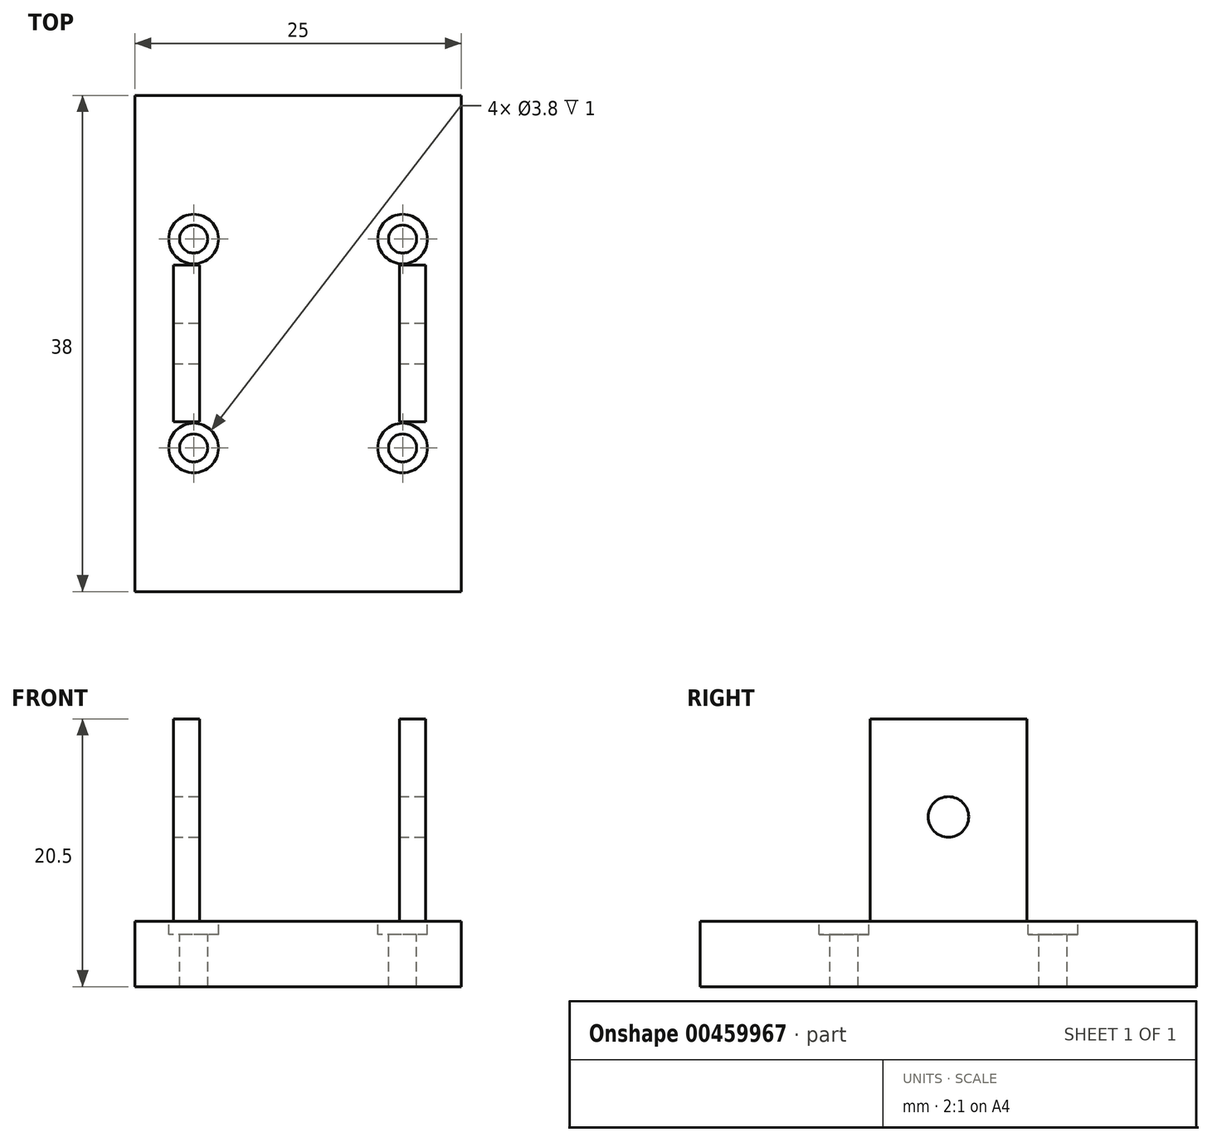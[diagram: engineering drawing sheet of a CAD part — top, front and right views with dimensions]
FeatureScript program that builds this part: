
annotation { "Feature Type Name" : "Feature", "Feature Type Description" : "" }
export const myFeature = defineFeature(function(context is Context, id is Id, definition is map)
    precondition{}
    {
        {
            var Q0;
            Q0=qCreatedBy(makeId("Top.planeOp"),FACE);
            var sketch = newSketch(context, id + "F0", { "sketchPlane" : qUnion([Q0])});
            skLineSegment(sketch, "E0.bottom", {"start": v(-18.16, 26.84) * mm, "end": v(6.84, 26.84) * mm});
            skLineSegment(sketch, "E0.top", {"start": v(-18.16, -11.16) * mm, "end": v(6.84, -11.16) * mm});
            skLineSegment(sketch, "E0.left", {"start": v(-18.16, 26.84) * mm, "end": v(-18.16, -11.16) * mm});
            skLineSegment(sketch, "E0.right", {"start": v(6.84, 26.84) * mm, "end": v(6.84, -11.16) * mm});
            skSolve(sketch);
        }
        {
            var Q0;
            Q0=makeQuery(id+"F0.imprint","IMPRINT",FACE,{"disambiguationData":[TD([[makeQuery(id+"F0.imprint","IMPRINT",EDGE,{"derivedFrom":sQuery(id+"F0.wireOp",EDGE,"E0.bottom")}),-1.0]])]});
            extrude(context, id + "F1", {"entities" : qUnion([Q0]), "depth" : 5 * mm});
        }
        {
            var Q0;
            Q0=makeQuery(id+"F1.opExtrude","CAP_FACE",FACE,{"disambiguationData":[OSD([sQuery(id+"F0.wireOp",EDGE,"E0.bottom"),sQuery(id+"F0.wireOp",EDGE,"E0.top"),sQuery(id+"F0.wireOp",EDGE,"E0.left"),sQuery(id+"F0.wireOp",EDGE,"E0.right")])],"isStart":false});
            var sketch = newSketch(context, id + "F2", { "sketchPlane" : qUnion([Q0])});
            skPoint(sketch, "E1.centerSnap0", {"position": v(-18.16, 7.84) * mm});
            skCircle(sketch, "E2", {"center": v(-13.66, 15.84) * mm, "radius": 1.07 * mm});
            skCircle(sketch, "E3", {"center": v(2.34, 15.84) * mm, "radius": 1.07 * mm});
            skCircle(sketch, "E4", {"center": v(-13.66, -0.16) * mm, "radius": 1.07 * mm});
            skCircle(sketch, "E5", {"center": v(2.34, -0.16) * mm, "radius": 1.07 * mm});
            skLineSegment(sketch, "E6.bottom", {"start": v(-13.66, 15.84) * mm, "end": v(2.34, 15.84) * mm});
            skLineSegment(sketch, "E6.top", {"start": v(-13.66, -0.16) * mm, "end": v(2.34, -0.16) * mm});
            skLineSegment(sketch, "E6.left", {"start": v(-13.66, 15.84) * mm, "end": v(-13.66, -0.16) * mm});
            skLineSegment(sketch, "E6.right", {"start": v(2.34, 15.84) * mm, "end": v(2.34, -0.16) * mm});
            skSolve(sketch);
        }
        {
            var Q0;
            {var subQ0=sQuery(id+"F2.wireOp",EDGE,"7fE2m0a1-qSu8-JNNJ-dZt4-1u2iovesNatf");var subQ1=sQuery(id+"F2.wireOp",EDGE,"E3");var subQ2=makeQuery(id+"F2.imprint","INTERSECT",VERTEX,{"derivedFrom":[subQ1,subQ0]});Q0=makeQuery(id+"F2.imprint","IMPRINT",FACE,{"disambiguationData":[TD([[makeQuery(id+"F2.imprint","IMPRINT",EDGE,{"disambiguationData":[TD([[subQ2,1.0]])],"derivedFrom":subQ1}),1.0]])]});}
            var Q1;
            {var subQ0=sQuery(id+"F2.wireOp",EDGE,"7fE2m0a1-qSu8-JNNJ-dZt4-1u2iovesNatf");var subQ1=sQuery(id+"F2.wireOp",EDGE,"E3");var subQ2=makeQuery(id+"F2.imprint","INTERSECT",VERTEX,{"derivedFrom":[subQ1,subQ0]});Q1=makeQuery(id+"F2.imprint","IMPRINT",FACE,{"disambiguationData":[TD([[makeQuery(id+"F2.imprint","IMPRINT",EDGE,{"disambiguationData":[TD([[subQ2,-1.0]])],"derivedFrom":subQ1}),1.0]])]});}
            var Q2;
            {var subQ0=sQuery(id+"F2.wireOp",EDGE,"WQd2Qh7p-ENVo-NeKd-jbVU-tQCCQaMnz0CV");var subQ1=sQuery(id+"F2.wireOp",EDGE,"E4");var subQ2=makeQuery(id+"F2.imprint","INTERSECT",VERTEX,{"derivedFrom":[subQ1,subQ0]});Q2=makeQuery(id+"F2.imprint","IMPRINT",FACE,{"disambiguationData":[TD([[makeQuery(id+"F2.imprint","IMPRINT",EDGE,{"disambiguationData":[TD([[subQ2,1.0]])],"derivedFrom":subQ1}),1.0]])]});}
            var Q3;
            {var subQ0=sQuery(id+"F2.wireOp",EDGE,"WQd2Qh7p-ENVo-NeKd-jbVU-tQCCQaMnz0CV");var subQ1=sQuery(id+"F2.wireOp",EDGE,"E4");var subQ2=makeQuery(id+"F2.imprint","INTERSECT",VERTEX,{"derivedFrom":[subQ1,subQ0]});Q3=makeQuery(id+"F2.imprint","IMPRINT",FACE,{"disambiguationData":[TD([[makeQuery(id+"F2.imprint","IMPRINT",EDGE,{"disambiguationData":[TD([[subQ2,-1.0]])],"derivedFrom":subQ1}),1.0]])]});}
            var Q4;
            {var subQ0=sQuery(id+"F2.wireOp",EDGE,"7fE2m0a1-qSu8-JNNJ-dZt4-1u2iovesNatf");var subQ1=sQuery(id+"F2.wireOp",EDGE,"E5");var subQ2=makeQuery(id+"F2.imprint","INTERSECT",VERTEX,{"derivedFrom":[subQ1,subQ0]});Q4=makeQuery(id+"F2.imprint","IMPRINT",FACE,{"disambiguationData":[TD([[makeQuery(id+"F2.imprint","IMPRINT",EDGE,{"disambiguationData":[TD([[subQ2,-1.0]])],"derivedFrom":subQ1}),1.0]])]});}
            var Q5;
            {var subQ0=sQuery(id+"F2.wireOp",EDGE,"7fE2m0a1-qSu8-JNNJ-dZt4-1u2iovesNatf");var subQ1=sQuery(id+"F2.wireOp",EDGE,"E5");var subQ2=makeQuery(id+"F2.imprint","INTERSECT",VERTEX,{"derivedFrom":[subQ1,subQ0]});Q5=makeQuery(id+"F2.imprint","IMPRINT",FACE,{"disambiguationData":[TD([[makeQuery(id+"F2.imprint","IMPRINT",EDGE,{"disambiguationData":[TD([[subQ2,1.0]])],"derivedFrom":subQ1}),1.0]])]});}
            var Q6;
            {var subQ0=sQuery(id+"F2.wireOp",EDGE,"WQd2Qh7p-ENVo-NeKd-jbVU-tQCCQaMnz0CV");var subQ1=sQuery(id+"F2.wireOp",EDGE,"E2");var subQ2=makeQuery(id+"F2.imprint","INTERSECT",VERTEX,{"derivedFrom":[subQ1,subQ0]});Q6=makeQuery(id+"F2.imprint","IMPRINT",FACE,{"disambiguationData":[TD([[makeQuery(id+"F2.imprint","IMPRINT",EDGE,{"disambiguationData":[TD([[subQ2,1.0]])],"derivedFrom":subQ1}),1.0]])]});}
            var Q7;
            {var subQ0=sQuery(id+"F2.wireOp",EDGE,"WQd2Qh7p-ENVo-NeKd-jbVU-tQCCQaMnz0CV");var subQ1=sQuery(id+"F2.wireOp",EDGE,"E2");var subQ2=makeQuery(id+"F2.imprint","INTERSECT",VERTEX,{"derivedFrom":[subQ1,subQ0]});Q7=makeQuery(id+"F2.imprint","IMPRINT",FACE,{"disambiguationData":[TD([[makeQuery(id+"F2.imprint","IMPRINT",EDGE,{"disambiguationData":[TD([[subQ2,-1.0]])],"derivedFrom":subQ1}),1.0]])]});}
            extrude(context, id + "F3", {"entities" : qUnion([Q0, Q1, Q2, Q3, Q4, Q5, Q6, Q7]), "operationType" : NewBodyOperationType.REMOVE, "oppositeDirection" : true, "depth" : 5 * mm});
        }
        {
            var Q0;
            Q0=makeQuery(id+"F1.opExtrude","CAP_FACE",FACE,{"disambiguationData":[OSD([sQuery(id+"F0.wireOp",EDGE,"E0.bottom"),sQuery(id+"F0.wireOp",EDGE,"E0.top"),sQuery(id+"F0.wireOp",EDGE,"E0.left"),sQuery(id+"F0.wireOp",EDGE,"E0.right")])],"isStart":false});
            var sketch = newSketch(context, id + "F4", { "sketchPlane" : qUnion([Q0])});
            skLineSegment(sketch, "E7.left", {"start": v(-15.21, 1.84) * mm, "end": v(-15.21, 13.84) * mm});
            skLineSegment(sketch, "E7.right", {"start": v(-13.21, 1.84) * mm, "end": v(-13.21, 13.84) * mm});
            skLineSegment(sketch, "E8", {"start": v(-15.21, 1.84) * mm, "end": v(-13.21, 1.84) * mm});
            skLineSegment(sketch, "E9", {"start": v(-15.21, 13.84) * mm, "end": v(-13.21, 13.84) * mm});
            skLineSegment(sketch, "E10.bottom", {"start": v(2.09, 1.84) * mm, "end": v(4.09, 1.84) * mm});
            skLineSegment(sketch, "E10.top", {"start": v(2.09, 13.84) * mm, "end": v(4.09, 13.84) * mm});
            skLineSegment(sketch, "E10.left", {"start": v(2.09, 1.84) * mm, "end": v(2.09, 13.84) * mm});
            skLineSegment(sketch, "E10.right", {"start": v(4.09, 1.84) * mm, "end": v(4.09, 13.84) * mm});
            skLineSegment(sketch, "E11", {"start": v(-14.21, 13.84) * mm, "end": v(-14.21, 26.84) * mm});
            skLineSegment(sketch, "E12", {"start": v(3.09, 13.84) * mm, "end": v(3.09, 26.84) * mm});
            skLineSegment(sketch, "E13", {"start": v(-14.21, 1.84) * mm, "end": v(-14.21, -11.16) * mm});
            skSolve(sketch);
        }
        {
            var Q0;
            Q0=makeQuery(id+"F4.imprint","IMPRINT",FACE,{"disambiguationData":[TD([[makeQuery(id+"F4.imprint","IMPRINT",EDGE,{"derivedFrom":sQuery(id+"F4.wireOp",EDGE,"E7.right")}),1.0]])]});
            var Q1;
            {var subQ1=sQuery(id+"F4.wireOp",EDGE,"E10.bottom");Q1=makeQuery(id+"F4.imprint","IMPRINT",FACE,{"disambiguationData":[TD([[makeQuery(id+"F4.imprint","IMPRINT",EDGE,{"derivedFrom":subQ1}),1.0]])]});}
            extrude(context, id + "F5", {"entities" : qUnion([Q0, Q1]), "operationType" : NewBodyOperationType.ADD, "depth" : 15.5 * mm});
        }
        {
            var Q0;
            Q0=makeQuery(id+"F5.opExtrude","SWEPT_FACE",FACE,{"disambiguationData":[OSD([sQuery(id+"F4.wireOp",EDGE,"E10.right")])]});
            var sketch = newSketch(context, id + "F6", { "sketchPlane" : qUnion([Q0])});
            skCircle(sketch, "E14", {"center": v(7.84, 13) * mm, "radius": 1.55 * mm});
            skLineSegment(sketch, "E15", {"start": v(7.84, 20.5) * mm, "end": v(7.84, 5) * mm});
            skSolve(sketch);
        }
        {
            var Q0;
            Q0=makeQuery(id+"F6.imprint","IMPRINT",FACE,{"disambiguationData":[TD([[makeQuery(id+"F6.imprint","IMPRINT",EDGE,{"derivedFrom":sQuery(id+"F6.wireOp",EDGE,"3uZkWBOX-bpGN-jUaI-Mrz7-4DPWOAVQxaKu")}),1.0]])]});
            var Q1;
            Q1=makeQuery(id+"F6.imprint","IMPRINT",FACE,{"disambiguationData":[TD([[makeQuery(id+"F6.imprint","IMPRINT",EDGE,{"derivedFrom":sQuery(id+"F6.wireOp",EDGE,"E14")}),1.0]])]});
            extrude(context, id + "F7", {"entities" : qUnion([Q0, Q1]), "operationType" : NewBodyOperationType.REMOVE, "oppositeDirection" : true, "depth" : 25 * mm});
        }
        {
            var Q0;
            Q0=makeQuery(id+"F1.opExtrude","CAP_FACE",FACE,{"disambiguationData":[OSD([sQuery(id+"F0.wireOp",EDGE,"E0.bottom"),sQuery(id+"F0.wireOp",EDGE,"E0.top"),sQuery(id+"F0.wireOp",EDGE,"E0.left"),sQuery(id+"F0.wireOp",EDGE,"E0.right")])],"isStart":false});
            var sketch = newSketch(context, id + "F8", { "sketchPlane" : qUnion([Q0])});
            skCircle(sketch, "E16", {"center": v(-13.66, 15.84) * mm, "radius": 1.9 * mm});
            skCircle(sketch, "E17", {"center": v(2.34, 15.84) * mm, "radius": 1.9 * mm});
            skCircle(sketch, "E18", {"center": v(2.34, -0.16) * mm, "radius": 1.9 * mm});
            skCircle(sketch, "E19", {"center": v(-13.66, -0.16) * mm, "radius": 1.9 * mm});
            skSolve(sketch);
        }
        {
            var Q0;
            Q0 = qSketchRegion(id + "F8", true);
            extrude(context, id + "F9", {"entities" : qUnion([Q0]), "operationType" : NewBodyOperationType.REMOVE, "oppositeDirection" : true, "depth" : 1 * mm, "offsetDistance" : 25 * mm});
        }
    });
